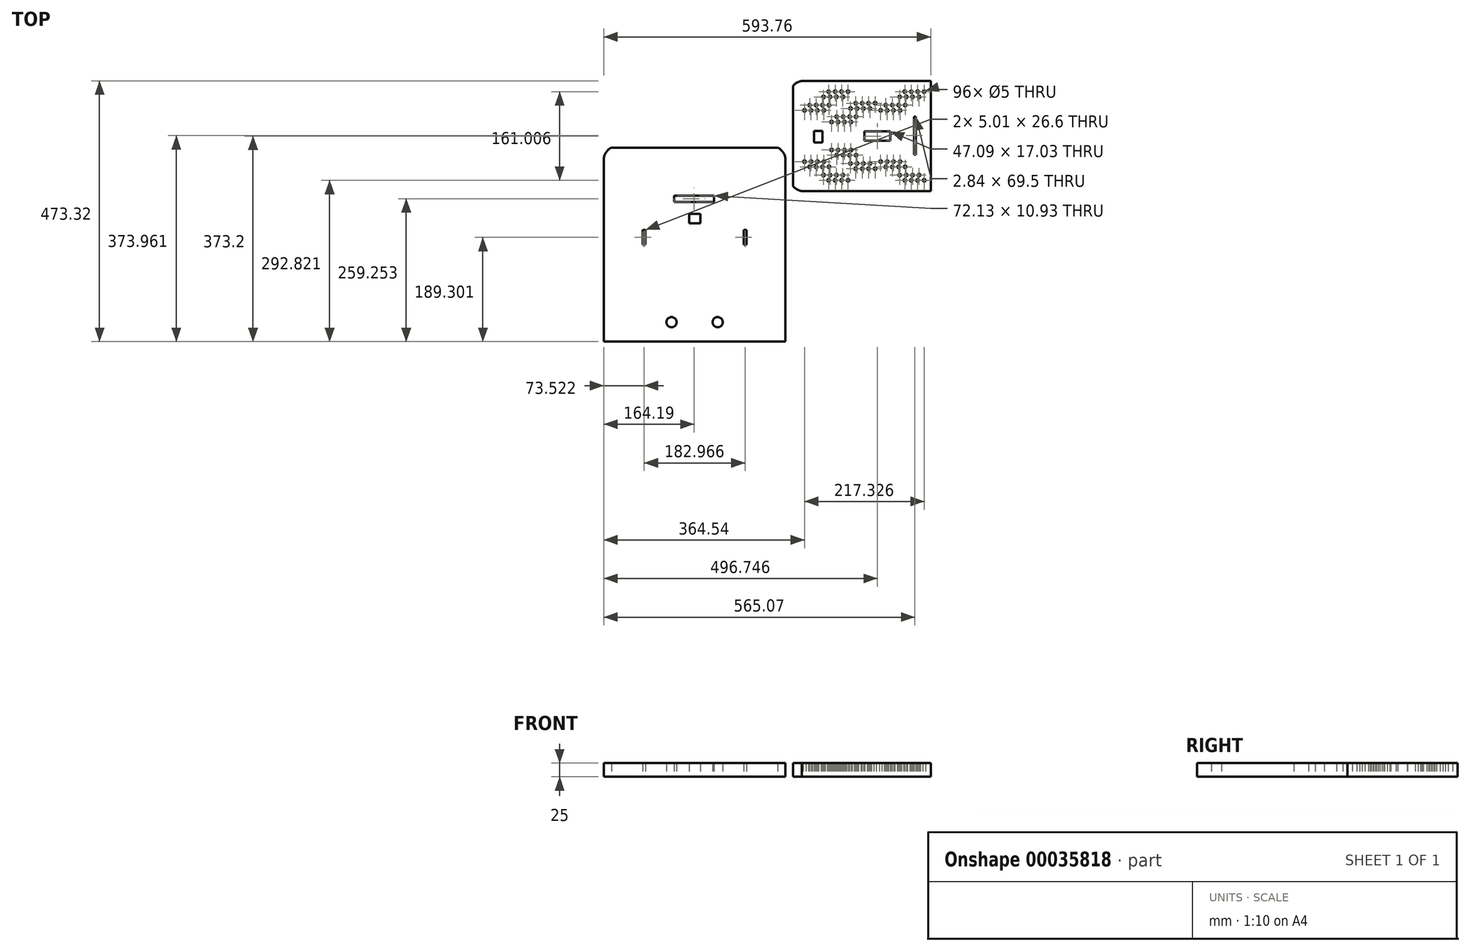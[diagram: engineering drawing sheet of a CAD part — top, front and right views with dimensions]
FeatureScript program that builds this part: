
annotation { "Feature Type Name" : "Feature", "Feature Type Description" : "" }
export const myFeature = defineFeature(function(context is Context, id is Id, definition is map)
    precondition{}
    {
        {
            var Q0;
            Q0=qCreatedBy(makeId("Top.planeOp"),FACE);
            var sketch = newSketch(context, id + "F0", { "sketchPlane" : qUnion([Q0])});
            skLineSegment(sketch, "E0.bottom", {"start": v(-545.13, 98.21) * mm, "end": v(-242.94, 98.21) * mm});
            skLineSegment(sketch, "E0.top", {"start": v(-559.04, -253.79) * mm, "end": v(-229.04, -253.79) * mm});
            skLineSegment(sketch, "E0.left", {"start": v(-559.04, 78.5) * mm, "end": v(-559.04, -253.79) * mm});
            skLineSegment(sketch, "E0.right", {"start": v(-229.04, 78.5) * mm, "end": v(-229.04, -253.79) * mm});
            skLineSegment(sketch, "E1", {"start": v(-394.04, 98.21) * mm, "end": v(-394.04, -253.79) * mm, "construction": true});
            skLineSegment(sketch, "E2.bottom", {"start": v(-430.92, 10.93) * mm, "end": v(-358.78, 10.93) * mm});
            skLineSegment(sketch, "E2.top", {"start": v(-430.92, 0) * mm, "end": v(-358.78, 0) * mm});
            skLineSegment(sketch, "E2.left", {"start": v(-430.92, 10.93) * mm, "end": v(-430.92, 0) * mm});
            skLineSegment(sketch, "E2.right", {"start": v(-358.78, 10.93) * mm, "end": v(-358.78, 0) * mm});
            skLineSegment(sketch, "E3.bottom", {"start": v(-403.87, -22.14) * mm, "end": v(-383.83, -22.14) * mm});
            skLineSegment(sketch, "E3.top", {"start": v(-403.87, -39.17) * mm, "end": v(-383.83, -39.17) * mm});
            skLineSegment(sketch, "E3.left", {"start": v(-403.87, -22.14) * mm, "end": v(-403.87, -39.17) * mm});
            skLineSegment(sketch, "E3.right", {"start": v(-383.83, -22.14) * mm, "end": v(-383.83, -39.17) * mm});
            skPoint(sketch, "E4.oppositeSnap0", {"position": v(-394.04, -77.79) * mm});
            skLineSegment(sketch, "E4.bottom", {"start": v(-488.02, -51.19) * mm, "end": v(-483.01, -51.19) * mm});
            skLineSegment(sketch, "E4.top", {"start": v(-488.02, -77.79) * mm, "end": v(-483.01, -77.79) * mm});
            skLineSegment(sketch, "E4.left", {"start": v(-488.02, -51.19) * mm, "end": v(-488.02, -77.79) * mm});
            skLineSegment(sketch, "E4.right", {"start": v(-483.01, -51.19) * mm, "end": v(-483.01, -77.79) * mm});
            skLineSegment(sketch, "E5.MirrorCS", {"start": v(-300.05, -51.19) * mm, "end": v(-305.06, -51.19) * mm});
            skLineSegment(sketch, "E6.MirrorCS", {"start": v(-300.05, -77.79) * mm, "end": v(-305.06, -77.79) * mm});
            skLineSegment(sketch, "E7.MirrorCS", {"start": v(-305.06, -51.19) * mm, "end": v(-305.06, -77.79) * mm});
            skLineSegment(sketch, "E8.MirrorCS", {"start": v(-300.05, -51.19) * mm, "end": v(-300.05, -77.79) * mm});
            skCircle(sketch, "E9", {"center": v(-435.93, -218.5) * mm, "radius": 9.24 * mm});
            skCircle(sketch, "E10.MirrorC", {"center": v(-352.14, -218.5) * mm, "radius": 9.24 * mm});
            skArc(sketch, "E11", {"start": v(-545.13, 98.21) * mm, "mid": v(-556.24, 87.33) * mm, "end": v(-559.04, 72.04) * mm});
            skArc(sketch, "E12.MirrorCS", {"start": v(-242.94, 98.21) * mm, "mid": v(-231.84, 87.33) * mm, "end": v(-229.04, 72.04) * mm});
            skSolve(sketch);
        }
        {
            var Q0;
            Q0=qCreatedBy(makeId("Top.planeOp"),FACE);
            var sketch = newSketch(context, id + "F1", { "sketchPlane" : qUnion([Q0])});
            skLineSegment(sketch, "E13.bottom", {"start": v(209.21, 93.3) * mm, "end": v(435.97, 93.3) * mm});
            skLineSegment(sketch, "E13.top", {"start": v(197.6, -206.7) * mm, "end": v(447.6, -206.7) * mm});
            skLineSegment(sketch, "E13.left", {"start": v(197.6, 76.54) * mm, "end": v(197.6, -206.7) * mm});
            skLineSegment(sketch, "E13.right", {"start": v(447.6, 76.54) * mm, "end": v(447.6, -206.7) * mm});
            skLineSegment(sketch, "E14", {"start": v(322.6, 93.3) * mm, "end": v(322.6, -206.7) * mm, "construction": true});
            skArc(sketch, "E15", {"start": v(209.21, 93.3) * mm, "mid": v(201.12, 86.5) * mm, "end": v(197.6, 76.54) * mm});
            skArc(sketch, "E16.MirrorCS", {"start": v(435.97, 93.3) * mm, "mid": v(444.06, 86.5) * mm, "end": v(447.6, 76.54) * mm});
            skCircle(sketch, "E17", {"center": v(230.31, 68.44) * mm, "radius": 2.5 * mm});
            skCircle(sketch, "E18", {"center": v(238.3, 68.31) * mm, "radius": 2.39 * mm});
            skCircle(sketch, "E19", {"center": v(245.98, 68.31) * mm, "radius": 2.5 * mm});
            skCircle(sketch, "E20", {"center": v(253.65, 68.31) * mm, "radius": 2.5 * mm});
            skCircle(sketch, "E21", {"center": v(246.06, 61.43) * mm, "radius": 2.5 * mm});
            skCircle(sketch, "E22", {"center": v(222.72, 61.56) * mm, "radius": 2.5 * mm});
            skCircle(sketch, "E23", {"center": v(230.71, 61.43) * mm, "radius": 2.39 * mm});
            skCircle(sketch, "E24", {"center": v(238.39, 61.43) * mm, "radius": 2.5 * mm});
            skCircle(sketch, "E25", {"center": v(238.66, 54.03) * mm, "radius": 2.5 * mm});
            skCircle(sketch, "E26", {"center": v(215.32, 54.16) * mm, "radius": 2.5 * mm});
            skCircle(sketch, "E27", {"center": v(223.31, 54.03) * mm, "radius": 2.39 * mm});
            skCircle(sketch, "E28", {"center": v(230.99, 54.03) * mm, "radius": 2.5 * mm});
            skCircle(sketch, "E29", {"center": v(278.95, 60.88) * mm, "radius": 2.5 * mm});
            skCircle(sketch, "E30", {"center": v(255.6, 61.01) * mm, "radius": 2.5 * mm});
            skCircle(sketch, "E31", {"center": v(263.6, 60.88) * mm, "radius": 2.39 * mm});
            skCircle(sketch, "E32", {"center": v(271.27, 60.88) * mm, "radius": 2.5 * mm});
            skCircle(sketch, "E33", {"center": v(285.25, 68.28) * mm, "radius": 2.5 * mm});
            skCircle(sketch, "E34", {"center": v(261.9, 68.41) * mm, "radius": 2.5 * mm});
            skCircle(sketch, "E35", {"center": v(269.9, 68.28) * mm, "radius": 2.39 * mm});
            skCircle(sketch, "E36", {"center": v(277.58, 68.28) * mm, "radius": 2.5 * mm});
            skCircle(sketch, "E37", {"center": v(281.41, 75.4) * mm, "radius": 2.5 * mm});
            skCircle(sketch, "E38", {"center": v(258.07, 75.54) * mm, "radius": 2.5 * mm});
            skCircle(sketch, "E39", {"center": v(266.07, 75.4) * mm, "radius": 2.39 * mm});
            skCircle(sketch, "E40", {"center": v(273.74, 75.4) * mm, "radius": 2.5 * mm});
            skCircle(sketch, "E41", {"center": v(296.4, 75.17) * mm, "radius": 2.5 * mm});
            skCircle(sketch, "E42", {"center": v(288.73, 75.17) * mm, "radius": 2.5 * mm});
            skCircle(sketch, "E43", {"center": v(260.89, 32.8) * mm, "radius": 2.5 * mm});
            skCircle(sketch, "E44", {"center": v(295.39, 39.55) * mm, "radius": 2.5 * mm});
            skCircle(sketch, "E45", {"center": v(262.58, 25.27) * mm, "radius": 2.39 * mm});
            skCircle(sketch, "E46", {"center": v(257.05, 39.92) * mm, "radius": 2.5 * mm});
            skCircle(sketch, "E47", {"center": v(280.4, 39.8) * mm, "radius": 2.5 * mm});
            skCircle(sketch, "E48", {"center": v(254.59, 25.4) * mm, "radius": 2.5 * mm});
            skCircle(sketch, "E49", {"center": v(245.04, 25.82) * mm, "radius": 2.5 * mm});
            skCircle(sketch, "E50", {"center": v(229.7, 25.82) * mm, "radius": 2.39 * mm});
            skCircle(sketch, "E51", {"center": v(272.72, 39.8) * mm, "radius": 2.5 * mm});
            skCircle(sketch, "E52", {"center": v(229.3, 32.83) * mm, "radius": 2.5 * mm});
            skCircle(sketch, "E53", {"center": v(237.64, 18.42) * mm, "radius": 2.5 * mm});
            skCircle(sketch, "E54", {"center": v(237.36, 25.82) * mm, "radius": 2.5 * mm});
            skCircle(sketch, "E55", {"center": v(244.96, 32.7) * mm, "radius": 2.5 * mm});
            skCircle(sketch, "E56", {"center": v(277.93, 25.27) * mm, "radius": 2.5 * mm});
            skCircle(sketch, "E57", {"center": v(229.96, 18.42) * mm, "radius": 2.5 * mm});
            skCircle(sketch, "E58", {"center": v(252.63, 32.7) * mm, "radius": 2.5 * mm});
            skCircle(sketch, "E59", {"center": v(270.25, 25.27) * mm, "radius": 2.5 * mm});
            skCircle(sketch, "E60", {"center": v(214.3, 18.55) * mm, "radius": 2.5 * mm});
            skCircle(sketch, "E61", {"center": v(287.71, 39.55) * mm, "radius": 2.5 * mm});
            skCircle(sketch, "E62", {"center": v(265.04, 39.8) * mm, "radius": 2.39 * mm});
            skCircle(sketch, "E63", {"center": v(276.55, 32.67) * mm, "radius": 2.5 * mm});
            skCircle(sketch, "E64", {"center": v(221.7, 25.95) * mm, "radius": 2.5 * mm});
            skCircle(sketch, "E65", {"center": v(268.88, 32.67) * mm, "radius": 2.39 * mm});
            skCircle(sketch, "E66", {"center": v(237.28, 32.7) * mm, "radius": 2.39 * mm});
            skCircle(sketch, "E67", {"center": v(222.3, 18.42) * mm, "radius": 2.39 * mm});
            skCircle(sketch, "E68", {"center": v(284.23, 32.67) * mm, "radius": 2.5 * mm});
            skCircle(sketch, "E69", {"center": v(259.78, -7.02) * mm, "radius": 2.5 * mm});
            skCircle(sketch, "E70", {"center": v(294.27, -0.26) * mm, "radius": 2.5 * mm});
            skCircle(sketch, "E71", {"center": v(261.47, -14.54) * mm, "radius": 2.39 * mm});
            skCircle(sketch, "E72", {"center": v(255.94, 0.11) * mm, "radius": 2.5 * mm});
            skCircle(sketch, "E73", {"center": v(279.28, -0.02) * mm, "radius": 2.5 * mm});
            skCircle(sketch, "E74", {"center": v(253.47, -14.42) * mm, "radius": 2.5 * mm});
            skCircle(sketch, "E75", {"center": v(243.93, -14) * mm, "radius": 2.5 * mm});
            skCircle(sketch, "E76", {"center": v(228.58, -14) * mm, "radius": 2.39 * mm});
            skCircle(sketch, "E77", {"center": v(271.6, -0.02) * mm, "radius": 2.5 * mm});
            skCircle(sketch, "E78", {"center": v(228.18, -6.98) * mm, "radius": 2.5 * mm});
            skCircle(sketch, "E79", {"center": v(236.53, -21.4) * mm, "radius": 2.5 * mm});
            skCircle(sketch, "E80", {"center": v(236.25, -14) * mm, "radius": 2.5 * mm});
            skCircle(sketch, "E81", {"center": v(243.85, -7.11) * mm, "radius": 2.5 * mm});
            skCircle(sketch, "E82", {"center": v(276.81, -14.54) * mm, "radius": 2.5 * mm});
            skCircle(sketch, "E83", {"center": v(228.85, -21.4) * mm, "radius": 2.5 * mm});
            skCircle(sketch, "E84", {"center": v(251.52, -7.11) * mm, "radius": 2.5 * mm});
            skCircle(sketch, "E85", {"center": v(269.14, -14.54) * mm, "radius": 2.5 * mm});
            skCircle(sketch, "E86", {"center": v(213.19, -21.27) * mm, "radius": 2.5 * mm});
            skCircle(sketch, "E87", {"center": v(286.6, -0.26) * mm, "radius": 2.5 * mm});
            skCircle(sketch, "E88", {"center": v(263.93, -0.02) * mm, "radius": 2.39 * mm});
            skCircle(sketch, "E89", {"center": v(275.44, -7.14) * mm, "radius": 2.5 * mm});
            skCircle(sketch, "E90", {"center": v(220.59, -13.87) * mm, "radius": 2.5 * mm});
            skCircle(sketch, "E91", {"center": v(267.77, -7.14) * mm, "radius": 2.39 * mm});
            skCircle(sketch, "E92", {"center": v(236.17, -7.11) * mm, "radius": 2.39 * mm});
            skCircle(sketch, "E93", {"center": v(221.18, -21.4) * mm, "radius": 2.39 * mm});
            skCircle(sketch, "E94", {"center": v(283.12, -7.14) * mm, "radius": 2.5 * mm});
            skCircle(sketch, "E95", {"center": v(259.12, -44.82) * mm, "radius": 2.5 * mm});
            skCircle(sketch, "E96", {"center": v(293.62, -38.07) * mm, "radius": 2.5 * mm});
            skCircle(sketch, "E97", {"center": v(260.81, -52.35) * mm, "radius": 2.39 * mm});
            skCircle(sketch, "E98", {"center": v(255.29, -37.7) * mm, "radius": 2.5 * mm});
            skCircle(sketch, "E99", {"center": v(278.63, -37.82) * mm, "radius": 2.5 * mm});
            skCircle(sketch, "E100", {"center": v(252.82, -52.22) * mm, "radius": 2.5 * mm});
            skCircle(sketch, "E101", {"center": v(243.27, -51.8) * mm, "radius": 2.5 * mm});
            skCircle(sketch, "E102", {"center": v(227.93, -51.8) * mm, "radius": 2.39 * mm});
            skCircle(sketch, "E103", {"center": v(270.95, -37.82) * mm, "radius": 2.5 * mm});
            skCircle(sketch, "E104", {"center": v(227.53, -44.79) * mm, "radius": 2.5 * mm});
            skCircle(sketch, "E105", {"center": v(235.87, -59.2) * mm, "radius": 2.5 * mm});
            skCircle(sketch, "E106", {"center": v(235.6, -51.8) * mm, "radius": 2.5 * mm});
            skCircle(sketch, "E107", {"center": v(243.2, -44.92) * mm, "radius": 2.5 * mm});
            skCircle(sketch, "E108", {"center": v(276.16, -52.35) * mm, "radius": 2.5 * mm});
            skCircle(sketch, "E109", {"center": v(228.2, -59.2) * mm, "radius": 2.5 * mm});
            skCircle(sketch, "E110", {"center": v(250.87, -44.92) * mm, "radius": 2.5 * mm});
            skCircle(sketch, "E111", {"center": v(268.49, -52.35) * mm, "radius": 2.5 * mm});
            skCircle(sketch, "E112", {"center": v(212.53, -59.07) * mm, "radius": 2.5 * mm});
            skCircle(sketch, "E113", {"center": v(285.95, -38.07) * mm, "radius": 2.5 * mm});
            skCircle(sketch, "E114", {"center": v(263.28, -37.82) * mm, "radius": 2.39 * mm});
            skCircle(sketch, "E115", {"center": v(274.8, -44.95) * mm, "radius": 2.5 * mm});
            skCircle(sketch, "E116", {"center": v(219.93, -51.67) * mm, "radius": 2.5 * mm});
            skCircle(sketch, "E117", {"center": v(267.12, -44.95) * mm, "radius": 2.39 * mm});
            skCircle(sketch, "E118", {"center": v(235.52, -44.92) * mm, "radius": 2.39 * mm});
            skCircle(sketch, "E119", {"center": v(220.53, -59.2) * mm, "radius": 2.39 * mm});
            skCircle(sketch, "E120", {"center": v(282.46, -44.95) * mm, "radius": 2.5 * mm});
            skCircle(sketch, "E121", {"center": v(262.06, -143.9) * mm, "radius": 2.5 * mm});
            skCircle(sketch, "E122", {"center": v(296.55, -137.14) * mm, "radius": 2.5 * mm});
            skCircle(sketch, "E123", {"center": v(263.75, -151.43) * mm, "radius": 2.39 * mm});
            skCircle(sketch, "E124", {"center": v(258.22, -136.77) * mm, "radius": 2.5 * mm});
            skCircle(sketch, "E125", {"center": v(281.56, -136.9) * mm, "radius": 2.5 * mm});
            skCircle(sketch, "E126", {"center": v(255.75, -151.3) * mm, "radius": 2.5 * mm});
            skCircle(sketch, "E127", {"center": v(246.2, -150.88) * mm, "radius": 2.5 * mm});
            skCircle(sketch, "E128", {"center": v(230.86, -150.88) * mm, "radius": 2.39 * mm});
            skCircle(sketch, "E129", {"center": v(273.89, -136.9) * mm, "radius": 2.5 * mm});
            skCircle(sketch, "E130", {"center": v(230.46, -143.87) * mm, "radius": 2.5 * mm});
            skCircle(sketch, "E131", {"center": v(238.8, -158.28) * mm, "radius": 2.5 * mm});
            skCircle(sketch, "E132", {"center": v(238.53, -150.88) * mm, "radius": 2.5 * mm});
            skCircle(sketch, "E133", {"center": v(246.13, -144) * mm, "radius": 2.5 * mm});
            skCircle(sketch, "E134", {"center": v(279.1, -151.43) * mm, "radius": 2.5 * mm});
            skCircle(sketch, "E135", {"center": v(231.13, -158.28) * mm, "radius": 2.5 * mm});
            skCircle(sketch, "E136", {"center": v(253.8, -144) * mm, "radius": 2.5 * mm});
            skCircle(sketch, "E137", {"center": v(271.42, -151.43) * mm, "radius": 2.5 * mm});
            skCircle(sketch, "E138", {"center": v(215.47, -158.15) * mm, "radius": 2.5 * mm});
            skCircle(sketch, "E139", {"center": v(288.88, -137.14) * mm, "radius": 2.5 * mm});
            skCircle(sketch, "E140", {"center": v(266.21, -136.9) * mm, "radius": 2.39 * mm});
            skCircle(sketch, "E141", {"center": v(277.72, -144.03) * mm, "radius": 2.5 * mm});
            skCircle(sketch, "E142", {"center": v(222.87, -150.75) * mm, "radius": 2.5 * mm});
            skCircle(sketch, "E143", {"center": v(270.05, -144.03) * mm, "radius": 2.39 * mm});
            skCircle(sketch, "E144", {"center": v(238.45, -144) * mm, "radius": 2.39 * mm});
            skCircle(sketch, "E145", {"center": v(223.46, -158.28) * mm, "radius": 2.39 * mm});
            skCircle(sketch, "E146", {"center": v(285.4, -144.03) * mm, "radius": 2.5 * mm});
            skCircle(sketch, "E147", {"center": v(231.11, -106.06) * mm, "radius": 2.5 * mm});
            skCircle(sketch, "E148", {"center": v(289.53, -99.34) * mm, "radius": 2.5 * mm});
            skCircle(sketch, "E149", {"center": v(264.4, -113.62) * mm, "radius": 2.39 * mm});
            skCircle(sketch, "E150", {"center": v(286.05, -106.22) * mm, "radius": 2.5 * mm});
            skCircle(sketch, "E151", {"center": v(254.45, -106.19) * mm, "radius": 2.5 * mm});
            skCircle(sketch, "E152", {"center": v(246.86, -113.07) * mm, "radius": 2.5 * mm});
            skCircle(sketch, "E153", {"center": v(279.75, -113.62) * mm, "radius": 2.5 * mm});
            skCircle(sketch, "E154", {"center": v(239.1, -106.19) * mm, "radius": 2.39 * mm});
            skCircle(sketch, "E155", {"center": v(231.51, -113.07) * mm, "radius": 2.39 * mm});
            skCircle(sketch, "E156", {"center": v(224.11, -120.47) * mm, "radius": 2.39 * mm});
            skCircle(sketch, "E157", {"center": v(274.54, -99.1) * mm, "radius": 2.5 * mm});
            skCircle(sketch, "E158", {"center": v(272.07, -113.62) * mm, "radius": 2.5 * mm});
            skCircle(sketch, "E159", {"center": v(262.7, -106.1) * mm, "radius": 2.5 * mm});
            skCircle(sketch, "E160", {"center": v(216.12, -120.34) * mm, "radius": 2.5 * mm});
            skCircle(sketch, "E161", {"center": v(297.2, -99.34) * mm, "radius": 2.5 * mm});
            skCircle(sketch, "E162", {"center": v(239.46, -120.47) * mm, "radius": 2.5 * mm});
            skCircle(sketch, "E163", {"center": v(266.87, -99.1) * mm, "radius": 2.39 * mm});
            skCircle(sketch, "E164", {"center": v(258.87, -98.97) * mm, "radius": 2.5 * mm});
            skCircle(sketch, "E165", {"center": v(239.19, -113.07) * mm, "radius": 2.5 * mm});
            skCircle(sketch, "E166", {"center": v(256.4, -113.5) * mm, "radius": 2.5 * mm});
            skCircle(sketch, "E167", {"center": v(223.52, -112.94) * mm, "radius": 2.5 * mm});
            skCircle(sketch, "E168", {"center": v(231.79, -120.47) * mm, "radius": 2.5 * mm});
            skCircle(sketch, "E169", {"center": v(246.78, -106.19) * mm, "radius": 2.5 * mm});
            skCircle(sketch, "E170", {"center": v(270.7, -106.22) * mm, "radius": 2.39 * mm});
            skCircle(sketch, "E171", {"center": v(278.38, -106.22) * mm, "radius": 2.5 * mm});
            skCircle(sketch, "E172", {"center": v(282.21, -99.1) * mm, "radius": 2.5 * mm});
            skCircle(sketch, "E173.MirrorC", {"center": v(374.48, -106.22) * mm, "radius": 2.39 * mm});
            skCircle(sketch, "E174.MirrorC", {"center": v(376.3, 32.67) * mm, "radius": 2.39 * mm});
            skCircle(sketch, "E175.MirrorC", {"center": v(400.23, 32.7) * mm, "radius": 2.5 * mm});
            skCircle(sketch, "E176.MirrorC", {"center": v(391.38, -144) * mm, "radius": 2.5 * mm});
            skCircle(sketch, "E177.MirrorC", {"center": v(384.3, 32.8) * mm, "radius": 2.5 * mm});
            skCircle(sketch, "E178.MirrorC", {"center": v(402, -44.92) * mm, "radius": 2.5 * mm});
            skCircle(sketch, "E179.MirrorC", {"center": v(362.97, -99.1) * mm, "radius": 2.5 * mm});
            skCircle(sketch, "E180.MirrorC", {"center": v(367.46, -144.03) * mm, "radius": 2.5 * mm});
            skCircle(sketch, "E181.MirrorC", {"center": v(424, -21.4) * mm, "radius": 2.39 * mm});
            skCircle(sketch, "E182.MirrorC", {"center": v(380.14, 39.8) * mm, "radius": 2.39 * mm});
            skCircle(sketch, "E183.MirrorC", {"center": v(394.32, -44.92) * mm, "radius": 2.5 * mm});
            skCircle(sketch, "E184.MirrorC", {"center": v(409.58, -51.8) * mm, "radius": 2.5 * mm});
            skCircle(sketch, "E185.MirrorC", {"center": v(382.48, -106.1) * mm, "radius": 2.5 * mm});
            skCircle(sketch, "E186.MirrorC", {"center": v(375.13, -144.03) * mm, "radius": 2.39 * mm});
            skCircle(sketch, "E187.MirrorC", {"center": v(378.97, -136.9) * mm, "radius": 2.39 * mm});
            skCircle(sketch, "E188.MirrorC", {"center": v(386.06, -44.82) * mm, "radius": 2.5 * mm});
            skCircle(sketch, "E189.MirrorC", {"center": v(372.47, 39.8) * mm, "radius": 2.5 * mm});
            skCircle(sketch, "E190.MirrorC", {"center": v(364.8, 39.8) * mm, "radius": 2.5 * mm});
            skCircle(sketch, "E191.MirrorC", {"center": v(392.55, 32.7) * mm, "radius": 2.5 * mm});
            skCircle(sketch, "E192.MirrorC", {"center": v(368.63, 32.67) * mm, "radius": 2.5 * mm});
            skCircle(sketch, "E193.MirrorC", {"center": v(373.76, -151.43) * mm, "radius": 2.5 * mm});
            skCircle(sketch, "E194.MirrorC", {"center": v(398.4, -106.19) * mm, "radius": 2.5 * mm});
            skCircle(sketch, "E195.MirrorC", {"center": v(365.9, -0.02) * mm, "radius": 2.5 * mm});
            skCircle(sketch, "E196.MirrorC", {"center": v(369.74, -7.14) * mm, "radius": 2.5 * mm});
            skCircle(sketch, "E197.MirrorC", {"center": v(383.13, -143.9) * mm, "radius": 2.5 * mm});
            skCircle(sketch, "E198.MirrorC", {"center": v(415.22, 18.42) * mm, "radius": 2.5 * mm});
            skCircle(sketch, "E199.MirrorC", {"center": v(414.72, -143.87) * mm, "radius": 2.5 * mm});
            skCircle(sketch, "E200.MirrorC", {"center": v(415.5, 25.82) * mm, "radius": 2.39 * mm});
            skCircle(sketch, "E201.MirrorC", {"center": v(407.9, 32.7) * mm, "radius": 2.39 * mm});
            skCircle(sketch, "E202.MirrorC", {"center": v(398.33, -113.07) * mm, "radius": 2.5 * mm});
            skCircle(sketch, "E203.MirrorC", {"center": v(413.4, -120.47) * mm, "radius": 2.5 * mm});
            skCircle(sketch, "E204.MirrorC", {"center": v(371.45, 75.4) * mm, "radius": 2.5 * mm});
            skCircle(sketch, "E205.MirrorC", {"center": v(409.66, -44.92) * mm, "radius": 2.39 * mm});
            skCircle(sketch, "E206.MirrorC", {"center": v(366.8, -106.22) * mm, "radius": 2.5 * mm});
            skCircle(sketch, "E207.MirrorC", {"center": v(377.42, -7.14) * mm, "radius": 2.39 * mm});
            skCircle(sketch, "E208.MirrorC", {"center": v(390.73, -106.19) * mm, "radius": 2.5 * mm});
            skCircle(sketch, "E209.MirrorC", {"center": v(399.06, -144) * mm, "radius": 2.5 * mm});
            skCircle(sketch, "E210.MirrorC", {"center": v(406.8, 61.43) * mm, "radius": 2.5 * mm});
            skCircle(sketch, "E211.MirrorC", {"center": v(406, -113.07) * mm, "radius": 2.5 * mm});
            skCircle(sketch, "E212.MirrorC", {"center": v(413.67, -113.07) * mm, "radius": 2.39 * mm});
            skCircle(sketch, "E213.MirrorC", {"center": v(406.73, -144) * mm, "radius": 2.39 * mm});
            skCircle(sketch, "E214.MirrorC", {"center": v(414.32, -150.88) * mm, "radius": 2.39 * mm});
            skCircle(sketch, "E215.MirrorC", {"center": v(359.94, 68.28) * mm, "radius": 2.5 * mm});
            skCircle(sketch, "E216.MirrorC", {"center": v(384.37, -52.35) * mm, "radius": 2.39 * mm});
            skCircle(sketch, "E217.MirrorC", {"center": v(401.34, -7.11) * mm, "radius": 2.5 * mm});
            skCircle(sketch, "E218.MirrorC", {"center": v(400.15, 25.82) * mm, "radius": 2.5 * mm});
            skCircle(sketch, "E219.MirrorC", {"center": v(347.98, -99.34) * mm, "radius": 2.5 * mm});
            skCircle(sketch, "E220.MirrorC", {"center": v(421.72, -158.28) * mm, "radius": 2.39 * mm});
            skCircle(sketch, "E221.MirrorC", {"center": v(371.3, -136.9) * mm, "radius": 2.5 * mm});
            skCircle(sketch, "E222.MirrorC", {"center": v(359.24, -38.07) * mm, "radius": 2.5 * mm});
            skCircle(sketch, "E223.MirrorC", {"center": v(383.28, 68.41) * mm, "radius": 2.5 * mm});
            skCircle(sketch, "E224.MirrorC", {"center": v(379.12, 75.4) * mm, "radius": 2.39 * mm});
            skCircle(sketch, "E225.MirrorC", {"center": v(421.67, -112.94) * mm, "radius": 2.5 * mm});
            skCircle(sketch, "E226.MirrorC", {"center": v(417.26, -51.8) * mm, "radius": 2.39 * mm});
            skCircle(sketch, "E227.MirrorC", {"center": v(417.66, -44.79) * mm, "radius": 2.5 * mm});
            skCircle(sketch, "E228.MirrorC", {"center": v(381.25, -0.02) * mm, "radius": 2.39 * mm});
            skCircle(sketch, "E229.MirrorC", {"center": v(365.44, -113.62) * mm, "radius": 2.5 * mm});
            skCircle(sketch, "E230.MirrorC", {"center": v(429.72, -158.15) * mm, "radius": 2.5 * mm});
            skCircle(sketch, "E231.MirrorC", {"center": v(421.87, 54.03) * mm, "radius": 2.39 * mm});
            skCircle(sketch, "E232.MirrorC", {"center": v(381.44, -151.43) * mm, "radius": 2.39 * mm});
            skCircle(sketch, "E233.MirrorC", {"center": v(369.02, -52.35) * mm, "radius": 2.5 * mm});
            skCircle(sketch, "E234.MirrorC", {"center": v(409.01, -7.11) * mm, "radius": 2.39 * mm});
            skCircle(sketch, "E235.MirrorC", {"center": v(416.6, -14) * mm, "radius": 2.39 * mm});
            skCircle(sketch, "E236.MirrorC", {"center": v(430.89, 18.55) * mm, "radius": 2.5 * mm});
            skCircle(sketch, "E237.MirrorC", {"center": v(349.8, 39.55) * mm, "radius": 2.5 * mm});
            skCircle(sketch, "E238.MirrorC", {"center": v(370.65, -99.1) * mm, "radius": 2.5 * mm});
            skCircle(sketch, "E239.MirrorC", {"center": v(416.98, -59.2) * mm, "radius": 2.5 * mm});
            skCircle(sketch, "E240.MirrorC", {"center": v(373.58, -0.02) * mm, "radius": 2.5 * mm});
            skCircle(sketch, "E241.MirrorC", {"center": v(389.58, 61.01) * mm, "radius": 2.5 * mm});
            skCircle(sketch, "E242.MirrorC", {"center": v(389.43, -151.3) * mm, "radius": 2.5 * mm});
            skCircle(sketch, "E243.MirrorC", {"center": v(362.07, -7.14) * mm, "radius": 2.5 * mm});
            skCircle(sketch, "E244.MirrorC", {"center": v(417, -6.98) * mm, "radius": 2.5 * mm});
            skCircle(sketch, "E245.MirrorC", {"center": v(373.11, -113.62) * mm, "radius": 2.5 * mm});
            skCircle(sketch, "E246.MirrorC", {"center": v(348.63, -137.14) * mm, "radius": 2.5 * mm});
            skCircle(sketch, "E247.MirrorC", {"center": v(370.4, -44.95) * mm, "radius": 2.5 * mm});
            skCircle(sketch, "E248.MirrorC", {"center": v(408.66, -21.4) * mm, "radius": 2.5 * mm});
            skCircle(sketch, "E249.MirrorC", {"center": v(424.6, -13.87) * mm, "radius": 2.5 * mm});
            skCircle(sketch, "E250.MirrorC", {"center": v(392.36, -52.22) * mm, "radius": 2.5 * mm});
            skCircle(sketch, "E251.MirrorC", {"center": v(367.6, 68.28) * mm, "radius": 2.5 * mm});
            skCircle(sketch, "E252.MirrorC", {"center": v(360.96, 32.67) * mm, "radius": 2.5 * mm});
            skCircle(sketch, "E253.MirrorC", {"center": v(393.66, -7.11) * mm, "radius": 2.5 * mm});
            skCircle(sketch, "E254.MirrorC", {"center": v(391.71, -14.42) * mm, "radius": 2.5 * mm});
            skCircle(sketch, "E255.MirrorC", {"center": v(415.9, 32.83) * mm, "radius": 2.5 * mm});
            skCircle(sketch, "E256.MirrorC", {"center": v(388.13, 39.92) * mm, "radius": 2.5 * mm});
            skCircle(sketch, "E257.MirrorC", {"center": v(363.62, -136.9) * mm, "radius": 2.5 * mm});
            skCircle(sketch, "E258.MirrorC", {"center": v(366.24, 60.88) * mm, "radius": 2.5 * mm});
            skCircle(sketch, "E259.MirrorC", {"center": v(382.6, 25.27) * mm, "radius": 2.39 * mm});
            skCircle(sketch, "E260.MirrorC", {"center": v(357.47, 39.55) * mm, "radius": 2.5 * mm});
            skCircle(sketch, "E261.MirrorC", {"center": v(429.87, 54.16) * mm, "radius": 2.5 * mm});
            skCircle(sketch, "E262.MirrorC", {"center": v(414.2, 54.03) * mm, "radius": 2.5 * mm});
            skCircle(sketch, "E263.MirrorC", {"center": v(356.45, 75.17) * mm, "radius": 2.5 * mm});
            skCircle(sketch, "E264.MirrorC", {"center": v(421.07, -120.47) * mm, "radius": 2.39 * mm});
            skCircle(sketch, "E265.MirrorC", {"center": v(386.96, -136.77) * mm, "radius": 2.5 * mm});
            skCircle(sketch, "E266.MirrorC", {"center": v(406.38, -158.28) * mm, "radius": 2.5 * mm});
            skCircle(sketch, "E267.MirrorC", {"center": v(414.07, -106.06) * mm, "radius": 2.5 * mm});
            skCircle(sketch, "E268.MirrorC", {"center": v(378.32, -99.1) * mm, "radius": 2.39 * mm});
            skCircle(sketch, "E269.MirrorC", {"center": v(376.7, -52.35) * mm, "radius": 2.5 * mm});
            skCircle(sketch, "E270.MirrorC", {"center": v(398.98, -150.88) * mm, "radius": 2.5 * mm});
            skCircle(sketch, "E271.MirrorC", {"center": v(381.59, 60.88) * mm, "radius": 2.39 * mm});
            skCircle(sketch, "E272.MirrorC", {"center": v(422.9, 18.42) * mm, "radius": 2.39 * mm});
            skCircle(sketch, "E273.MirrorC", {"center": v(416.33, -21.4) * mm, "radius": 2.5 * mm});
            skCircle(sketch, "E274.MirrorC", {"center": v(366.56, -37.82) * mm, "radius": 2.5 * mm});
            skCircle(sketch, "E275.MirrorC", {"center": v(375.28, 68.28) * mm, "radius": 2.39 * mm});
            skCircle(sketch, "E276.MirrorC", {"center": v(409.31, -59.2) * mm, "radius": 2.5 * mm});
            skCircle(sketch, "E277.MirrorC", {"center": v(348.78, 75.17) * mm, "radius": 2.5 * mm});
            skCircle(sketch, "E278.MirrorC", {"center": v(381.9, -37.82) * mm, "radius": 2.39 * mm});
            skCircle(sketch, "E279.MirrorC", {"center": v(359.79, -144.03) * mm, "radius": 2.5 * mm});
            skCircle(sketch, "E280.MirrorC", {"center": v(405.73, -120.47) * mm, "radius": 2.5 * mm});
            skCircle(sketch, "E281.MirrorC", {"center": v(389.25, 0.11) * mm, "radius": 2.5 * mm});
            skCircle(sketch, "E282.MirrorC", {"center": v(362.72, -44.95) * mm, "radius": 2.5 * mm});
            skCircle(sketch, "E283.MirrorC", {"center": v(422.47, 61.56) * mm, "radius": 2.5 * mm});
            skCircle(sketch, "E284.MirrorC", {"center": v(367.26, 25.27) * mm, "radius": 2.5 * mm});
            skCircle(sketch, "E285.MirrorC", {"center": v(399.13, 61.43) * mm, "radius": 2.5 * mm});
            skCircle(sketch, "E286.MirrorC", {"center": v(391.53, 68.31) * mm, "radius": 2.5 * mm});
            skCircle(sketch, "E287.MirrorC", {"center": v(366.1, -151.43) * mm, "radius": 2.5 * mm});
            skCircle(sketch, "E288.MirrorC", {"center": v(399.2, 68.31) * mm, "radius": 2.5 * mm});
            skCircle(sketch, "E289.MirrorC", {"center": v(407.82, 25.82) * mm, "radius": 2.5 * mm});
            skCircle(sketch, "E290.MirrorC", {"center": v(387.11, 75.54) * mm, "radius": 2.5 * mm});
            skCircle(sketch, "E291.MirrorC", {"center": v(414.05, -158.28) * mm, "radius": 2.5 * mm});
            skCircle(sketch, "E292.MirrorC", {"center": v(383.72, -14.54) * mm, "radius": 2.39 * mm});
            skCircle(sketch, "E293.MirrorC", {"center": v(374.23, -37.82) * mm, "radius": 2.5 * mm});
            skCircle(sketch, "E294.MirrorC", {"center": v(422.32, -150.75) * mm, "radius": 2.5 * mm});
            skCircle(sketch, "E295.MirrorC", {"center": v(407.55, 18.42) * mm, "radius": 2.5 * mm});
            skCircle(sketch, "E296.MirrorC", {"center": v(376.05, -14.54) * mm, "radius": 2.5 * mm});
            skCircle(sketch, "E297.MirrorC", {"center": v(429.07, -120.34) * mm, "radius": 2.5 * mm});
            skCircle(sketch, "E298.MirrorC", {"center": v(408.93, -14) * mm, "radius": 2.5 * mm});
            skCircle(sketch, "E299.MirrorC", {"center": v(351.56, -38.07) * mm, "radius": 2.5 * mm});
            skCircle(sketch, "E300.MirrorC", {"center": v(423.49, 25.95) * mm, "radius": 2.5 * mm});
            skCircle(sketch, "E301.MirrorC", {"center": v(432, -21.27) * mm, "radius": 2.5 * mm});
            skCircle(sketch, "E302.MirrorC", {"center": v(401.91, -51.8) * mm, "radius": 2.5 * mm});
            skCircle(sketch, "E303.MirrorC", {"center": v(380.79, -113.62) * mm, "radius": 2.39 * mm});
            skCircle(sketch, "E304.MirrorC", {"center": v(425.25, -51.67) * mm, "radius": 2.5 * mm});
            skCircle(sketch, "E305.MirrorC", {"center": v(374.93, 25.27) * mm, "radius": 2.5 * mm});
            skCircle(sketch, "E306.MirrorC", {"center": v(373.91, 60.88) * mm, "radius": 2.5 * mm});
            skCircle(sketch, "E307.MirrorC", {"center": v(388.78, -113.5) * mm, "radius": 2.5 * mm});
            skCircle(sketch, "E308.MirrorC", {"center": v(350.91, -0.26) * mm, "radius": 2.5 * mm});
            skCircle(sketch, "E309.MirrorC", {"center": v(414.47, 61.43) * mm, "radius": 2.39 * mm});
            skCircle(sketch, "E310.MirrorC", {"center": v(368.37, -14.54) * mm, "radius": 2.5 * mm});
            skCircle(sketch, "E311.MirrorC", {"center": v(356.3, -137.14) * mm, "radius": 2.5 * mm});
            skCircle(sketch, "E312.MirrorC", {"center": v(424.66, -59.2) * mm, "radius": 2.39 * mm});
            skCircle(sketch, "E313.MirrorC", {"center": v(363.77, 75.4) * mm, "radius": 2.5 * mm});
            skCircle(sketch, "E314.MirrorC", {"center": v(355.65, -99.34) * mm, "radius": 2.5 * mm});
            skCircle(sketch, "E315.MirrorC", {"center": v(406.88, 68.31) * mm, "radius": 2.39 * mm});
            skCircle(sketch, "E316.MirrorC", {"center": v(414.87, 68.44) * mm, "radius": 2.5 * mm});
            skCircle(sketch, "E317.MirrorC", {"center": v(386.31, -98.97) * mm, "radius": 2.5 * mm});
            skCircle(sketch, "E318.MirrorC", {"center": v(406.65, -150.88) * mm, "radius": 2.5 * mm});
            skCircle(sketch, "E319.MirrorC", {"center": v(390.6, 25.4) * mm, "radius": 2.5 * mm});
            skCircle(sketch, "E320.MirrorC", {"center": v(401.26, -14) * mm, "radius": 2.5 * mm});
            skCircle(sketch, "E321.MirrorC", {"center": v(389.9, -37.7) * mm, "radius": 2.5 * mm});
            skCircle(sketch, "E322.MirrorC", {"center": v(406.53, 54.03) * mm, "radius": 2.5 * mm});
            skCircle(sketch, "E323.MirrorC", {"center": v(378.07, -44.95) * mm, "radius": 2.39 * mm});
            skCircle(sketch, "E324.MirrorC", {"center": v(432.65, -59.07) * mm, "radius": 2.5 * mm});
            skCircle(sketch, "E325.MirrorC", {"center": v(406.08, -106.19) * mm, "radius": 2.39 * mm});
            skCircle(sketch, "E326.MirrorC", {"center": v(359.14, -106.22) * mm, "radius": 2.5 * mm});
            skCircle(sketch, "E327.MirrorC", {"center": v(385.4, -7.02) * mm, "radius": 2.5 * mm});
            skCircle(sketch, "E328.MirrorC", {"center": v(358.59, -0.26) * mm, "radius": 2.5 * mm});
            skPoint(sketch, "E329.oppositeSnap0", {"position": v(322.6, -56.7) * mm});
            skLineSegment(sketch, "E329.bottom", {"start": v(315.94, -9.87) * mm, "end": v(328.97, -9.87) * mm});
            skLineSegment(sketch, "E329.top", {"start": v(315.94, -56.7) * mm, "end": v(328.97, -56.7) * mm});
            skLineSegment(sketch, "E329.left", {"start": v(315.94, -9.87) * mm, "end": v(315.94, -56.7) * mm});
            skLineSegment(sketch, "E329.right", {"start": v(328.97, -9.87) * mm, "end": v(328.97, -56.7) * mm});
            skLineSegment(sketch, "E330.bottom", {"start": v(306.81, -149.36) * mm, "end": v(337.45, -149.36) * mm});
            skLineSegment(sketch, "E330.top", {"start": v(306.81, -153.92) * mm, "end": v(337.45, -153.92) * mm});
            skLineSegment(sketch, "E330.left", {"start": v(306.81, -149.36) * mm, "end": v(306.81, -153.92) * mm});
            skLineSegment(sketch, "E330.right", {"start": v(337.45, -149.36) * mm, "end": v(337.45, -153.92) * mm});
            skLineSegment(sketch, "E331.bottom", {"start": v(289.21, -172.17) * mm, "end": v(352.44, -172.17) * mm});
            skLineSegment(sketch, "E331.top", {"start": v(289.21, -181.95) * mm, "end": v(352.44, -181.95) * mm});
            skLineSegment(sketch, "E331.left", {"start": v(289.21, -172.17) * mm, "end": v(289.21, -181.95) * mm});
            skLineSegment(sketch, "E331.right", {"start": v(352.44, -172.17) * mm, "end": v(352.44, -181.95) * mm});
            skLineSegment(sketch, "E332.bottom", {"start": v(246.2, -71.14) * mm, "end": v(284.65, -71.14) * mm});
            skLineSegment(sketch, "E332.top", {"start": v(246.2, -75.7) * mm, "end": v(284.65, -75.7) * mm});
            skLineSegment(sketch, "E332.left", {"start": v(246.2, -71.14) * mm, "end": v(246.2, -75.7) * mm});
            skLineSegment(sketch, "E332.right", {"start": v(284.65, -71.14) * mm, "end": v(284.65, -75.7) * mm});
            skLineSegment(sketch, "E333.MirrorCS", {"start": v(360.53, -71.14) * mm, "end": v(360.53, -75.7) * mm});
            skLineSegment(sketch, "E334.MirrorCS", {"start": v(399, -71.14) * mm, "end": v(399, -75.7) * mm});
            skLineSegment(sketch, "E335.MirrorCS", {"start": v(399, -71.14) * mm, "end": v(360.53, -71.14) * mm});
            skLineSegment(sketch, "E336.MirrorCS", {"start": v(399, -75.7) * mm, "end": v(360.53, -75.7) * mm});
            skSolve(sketch);
        }
        {
            var Q0;
            Q0=qCreatedBy(makeId("Top.planeOp"),FACE);
            var sketch = newSketch(context, id + "F2", { "sketchPlane" : qUnion([Q0])});
            skLineSegment(sketch, "E337.bottom", {"start": v(-199.27, 219.53) * mm, "end": v(34.72, 219.53) * mm});
            skLineSegment(sketch, "E337.top", {"start": v(-199.27, 19.53) * mm, "end": v(34.72, 19.53) * mm});
            skLineSegment(sketch, "E337.left", {"start": v(-215.28, 210.55) * mm, "end": v(-215.28, 28.52) * mm});
            skLineSegment(sketch, "E337.right", {"start": v(34.72, 219.53) * mm, "end": v(34.72, 19.53) * mm});
            skCircle(sketch, "E338.MirrorC", {"center": v(230, -11.5) * mm, "radius": 2.5 * mm});
            skCircle(sketch, "E339.MirrorC", {"center": v(249.15, 65.11) * mm, "radius": 2.5 * mm});
            skCircle(sketch, "E340.MirrorC", {"center": v(227.6, -1.94) * mm, "radius": 2.5 * mm});
            skCircle(sketch, "E341.MirrorC", {"center": v(218.19, -11.5) * mm, "radius": 2.5 * mm});
            skCircle(sketch, "E342.MirrorC", {"center": v(259.2, 50.21) * mm, "radius": 2.5 * mm});
            skCircle(sketch, "E343.MirrorC", {"center": v(270.37, 74.67) * mm, "radius": 2.5 * mm});
            skCircle(sketch, "E344.MirrorC", {"center": v(250.94, -1.94) * mm, "radius": 2.5 * mm});
            skCircle(sketch, "E345.MirrorC", {"center": v(276.45, -44.4) * mm, "radius": 2.5 * mm});
            skCircle(sketch, "E346.MirrorC", {"center": v(276.03, 12.96) * mm, "radius": 2.5 * mm});
            skCircle(sketch, "E347.MirrorC", {"center": v(226.44, 40.65) * mm, "radius": 2.5 * mm});
            skCircle(sketch, "E348.MirrorC", {"center": v(244.33, -78.4) * mm, "radius": 2.5 * mm});
            skCircle(sketch, "E349.MirrorC", {"center": v(260.95, 65.11) * mm, "radius": 2.5 * mm});
            skCircle(sketch, "E350.MirrorC", {"center": v(249.78, 40.65) * mm, "radius": 2.5 * mm});
            skCircle(sketch, "E351.MirrorC", {"center": v(253.33, -11.5) * mm, "radius": 2.5 * mm});
            skCircle(sketch, "E352.MirrorC", {"center": v(230.42, -68.85) * mm, "radius": 2.5 * mm});
            skCircle(sketch, "E353.MirrorC", {"center": v(252.7, 12.96) * mm, "radius": 2.5 * mm});
            skCircle(sketch, "E354.MirrorC", {"center": v(247.39, 50.21) * mm, "radius": 2.5 * mm});
            skCircle(sketch, "E355.MirrorC", {"center": v(267.03, -53.95) * mm, "radius": 2.5 * mm});
            skCircle(sketch, "E356.MirrorC", {"center": v(232.52, -78.4) * mm, "radius": 2.5 * mm});
            skCircle(sketch, "E357.MirrorC", {"center": v(284.29, 65.11) * mm, "radius": 2.5 * mm});
            skCircle(sketch, "E358.MirrorC", {"center": v(241.94, -68.85) * mm, "radius": 2.5 * mm});
            skCircle(sketch, "E359.MirrorC", {"center": v(253.12, -44.4) * mm, "radius": 2.5 * mm});
            skCircle(sketch, "E360.MirrorC", {"center": v(293.7, 74.67) * mm, "radius": 2.5 * mm});
            skCircle(sketch, "E361.MirrorC", {"center": v(214.64, 40.65) * mm, "radius": 2.5 * mm});
            skCircle(sketch, "E362.MirrorC", {"center": v(241.52, -11.5) * mm, "radius": 2.5 * mm});
            skCircle(sketch, "E363.MirrorC", {"center": v(243.7, -53.95) * mm, "radius": 2.5 * mm});
            skCircle(sketch, "E364.MirrorC", {"center": v(262.11, 22.52) * mm, "radius": 2.5 * mm});
            skCircle(sketch, "E365.MirrorC", {"center": v(239.41, -1.94) * mm, "radius": 2.5 * mm});
            skCircle(sketch, "E366.MirrorC", {"center": v(272.48, 65.11) * mm, "radius": 2.5 * mm});
            skCircle(sketch, "E367.MirrorC", {"center": v(262.75, -1.94) * mm, "radius": 2.5 * mm});
            skCircle(sketch, "E368.MirrorC", {"center": v(218.6, -68.85) * mm, "radius": 2.5 * mm});
            skCircle(sketch, "E369.MirrorC", {"center": v(287.84, 12.96) * mm, "radius": 2.5 * mm});
            skCircle(sketch, "E370.MirrorC", {"center": v(209.19, -78.4) * mm, "radius": 2.5 * mm});
            skCircle(sketch, "E371.MirrorC", {"center": v(285.45, 22.52) * mm, "radius": 2.5 * mm});
            skCircle(sketch, "E372.MirrorC", {"center": v(297.26, 22.52) * mm, "radius": 2.5 * mm});
            skCircle(sketch, "E373.MirrorC", {"center": v(253.75, -68.85) * mm, "radius": 2.5 * mm});
            skCircle(sketch, "E374.MirrorC", {"center": v(224.05, 50.21) * mm, "radius": 2.5 * mm});
            skCircle(sketch, "E375.MirrorC", {"center": v(258.56, 74.67) * mm, "radius": 2.5 * mm});
            skCircle(sketch, "E376.MirrorC", {"center": v(278.84, -53.95) * mm, "radius": 2.5 * mm});
            skCircle(sketch, "E377.MirrorC", {"center": v(273.92, 22.52) * mm, "radius": 2.5 * mm});
            skCircle(sketch, "E378.MirrorC", {"center": v(221, -78.4) * mm, "radius": 2.5 * mm});
            skCircle(sketch, "E379.MirrorC", {"center": v(288.26, -44.4) * mm, "radius": 2.5 * mm});
            skCircle(sketch, "E380.MirrorC", {"center": v(264.92, -44.4) * mm, "radius": 2.5 * mm});
            skCircle(sketch, "E381.MirrorC", {"center": v(255.5, -53.95) * mm, "radius": 2.5 * mm});
            skCircle(sketch, "E382.MirrorC", {"center": v(237.97, 40.65) * mm, "radius": 2.5 * mm});
            skCircle(sketch, "E383.MirrorC", {"center": v(281.9, 74.67) * mm, "radius": 2.5 * mm});
            skCircle(sketch, "E384.MirrorC", {"center": v(235.86, 50.21) * mm, "radius": 2.5 * mm});
            skCircle(sketch, "E385.MirrorC", {"center": v(264.5, 12.96) * mm, "radius": 2.5 * mm});
            skCircle(sketch, "E386.MirrorC", {"center": v(212.22, -129) * mm, "radius": 2.5 * mm});
            skCircle(sketch, "E387.MirrorC", {"center": v(281.87, -104.55) * mm, "radius": 2.5 * mm});
            skCircle(sketch, "E388.MirrorC", {"center": v(256.14, -94.99) * mm, "radius": 2.5 * mm});
            skCircle(sketch, "E389.MirrorC", {"center": v(233.44, -119.45) * mm, "radius": 2.5 * mm});
            skCircle(sketch, "E390.MirrorC", {"center": v(221.63, -119.45) * mm, "radius": 2.5 * mm});
            skCircle(sketch, "E391.MirrorC", {"center": v(244.97, -119.45) * mm, "radius": 2.5 * mm});
            skCircle(sketch, "E392.MirrorC", {"center": v(256.78, -119.45) * mm, "radius": 2.5 * mm});
            skCircle(sketch, "E393.MirrorC", {"center": v(270.06, -104.55) * mm, "radius": 2.5 * mm});
            skCircle(sketch, "E394.MirrorC", {"center": v(235.55, -129) * mm, "radius": 2.5 * mm});
            skCircle(sketch, "E395.MirrorC", {"center": v(258.53, -104.55) * mm, "radius": 2.5 * mm});
            skCircle(sketch, "E396.MirrorC", {"center": v(247.36, -129) * mm, "radius": 2.5 * mm});
            skCircle(sketch, "E397.MirrorC", {"center": v(267.95, -94.99) * mm, "radius": 2.5 * mm});
            skCircle(sketch, "E398.MirrorC", {"center": v(246.73, -104.55) * mm, "radius": 2.5 * mm});
            skCircle(sketch, "E399.MirrorC", {"center": v(291.29, -94.99) * mm, "radius": 2.5 * mm});
            skCircle(sketch, "E400.MirrorC", {"center": v(279.48, -94.99) * mm, "radius": 2.5 * mm});
            skCircle(sketch, "E401.MirrorC", {"center": v(224.02, -129) * mm, "radius": 2.5 * mm});
            skCircle(sketch, "E402.MirrorC", {"center": v(215.2, -180.83) * mm, "radius": 2.5 * mm});
            skCircle(sketch, "E403.MirrorC", {"center": v(284.85, -156.37) * mm, "radius": 2.5 * mm});
            skCircle(sketch, "E404.MirrorC", {"center": v(259.12, -146.82) * mm, "radius": 2.5 * mm});
            skCircle(sketch, "E405.MirrorC", {"center": v(236.42, -171.27) * mm, "radius": 2.5 * mm});
            skCircle(sketch, "E406.MirrorC", {"center": v(224.61, -171.27) * mm, "radius": 2.5 * mm});
            skCircle(sketch, "E407.MirrorC", {"center": v(247.95, -171.27) * mm, "radius": 2.5 * mm});
            skCircle(sketch, "E408.MirrorC", {"center": v(259.76, -171.27) * mm, "radius": 2.5 * mm});
            skCircle(sketch, "E409.MirrorC", {"center": v(273.04, -156.37) * mm, "radius": 2.5 * mm});
            skCircle(sketch, "E410.MirrorC", {"center": v(238.53, -180.83) * mm, "radius": 2.5 * mm});
            skCircle(sketch, "E411.MirrorC", {"center": v(261.51, -156.37) * mm, "radius": 2.5 * mm});
            skCircle(sketch, "E412.MirrorC", {"center": v(250.34, -180.83) * mm, "radius": 2.5 * mm});
            skCircle(sketch, "E413.MirrorC", {"center": v(270.93, -146.82) * mm, "radius": 2.5 * mm});
            skCircle(sketch, "E414.MirrorC", {"center": v(249.7, -156.37) * mm, "radius": 2.5 * mm});
            skCircle(sketch, "E415.MirrorC", {"center": v(294.27, -146.82) * mm, "radius": 2.5 * mm});
            skCircle(sketch, "E416.MirrorC", {"center": v(282.46, -146.82) * mm, "radius": 2.5 * mm});
            skCircle(sketch, "E417.MirrorC", {"center": v(227, -180.83) * mm, "radius": 2.5 * mm});
            skCircle(sketch, "E418.MirrorC", {"center": v(377.23, -94.99) * mm, "radius": 2.5 * mm});
            skCircle(sketch, "E419.MirrorC", {"center": v(374.25, -146.82) * mm, "radius": 2.5 * mm});
            skCircle(sketch, "E420.MirrorC", {"center": v(384.23, 65.11) * mm, "radius": 2.5 * mm});
            skCircle(sketch, "E421.MirrorC", {"center": v(405.77, -1.94) * mm, "radius": 2.5 * mm});
            skCircle(sketch, "E422.MirrorC", {"center": v(389.68, -53.95) * mm, "radius": 2.5 * mm});
            skCircle(sketch, "E423.MirrorC", {"center": v(394.85, -180.83) * mm, "radius": 2.5 * mm});
            skCircle(sketch, "E424.MirrorC", {"center": v(397.83, -129) * mm, "radius": 2.5 * mm});
            skCircle(sketch, "E425.MirrorC", {"center": v(400.85, -78.4) * mm, "radius": 2.5 * mm});
            skCircle(sketch, "E426.MirrorC", {"center": v(383.07, 22.52) * mm, "radius": 2.5 * mm});
            skCircle(sketch, "E427.MirrorC", {"center": v(380.26, -44.4) * mm, "radius": 2.5 * mm});
            skCircle(sketch, "E428.MirrorC", {"center": v(421.16, -129) * mm, "radius": 2.5 * mm});
            skCircle(sketch, "E429.MirrorC", {"center": v(418.18, -180.83) * mm, "radius": 2.5 * mm});
            skCircle(sketch, "E430.MirrorC", {"center": v(386.65, -104.55) * mm, "radius": 2.5 * mm});
            skCircle(sketch, "E431.MirrorC", {"center": v(383.67, -156.37) * mm, "radius": 2.5 * mm});
            skCircle(sketch, "E432.MirrorC", {"center": v(418.74, 40.65) * mm, "radius": 2.5 * mm});
            skCircle(sketch, "E433.MirrorC", {"center": v(401.49, -53.95) * mm, "radius": 2.5 * mm});
            skCircle(sketch, "E434.MirrorC", {"center": v(356.93, -44.4) * mm, "radius": 2.5 * mm});
            skCircle(sketch, "E435.MirrorC", {"center": v(371.26, 22.52) * mm, "radius": 2.5 * mm});
            skCircle(sketch, "E436.MirrorC", {"center": v(375.12, -104.55) * mm, "radius": 2.5 * mm});
            skCircle(sketch, "E437.MirrorC", {"center": v(372.15, -156.37) * mm, "radius": 2.5 * mm});
            skCircle(sketch, "E438.MirrorC", {"center": v(368.73, -44.4) * mm, "radius": 2.5 * mm});
            skCircle(sketch, "E439.MirrorC", {"center": v(430.55, 40.65) * mm, "radius": 2.5 * mm});
            skCircle(sketch, "E440.MirrorC", {"center": v(403.66, -11.5) * mm, "radius": 2.5 * mm});
            skCircle(sketch, "E441.MirrorC", {"center": v(369.16, 12.96) * mm, "radius": 2.5 * mm});
            skCircle(sketch, "E442.MirrorC", {"center": v(424.19, -78.4) * mm, "radius": 2.5 * mm});
            skCircle(sketch, "E443.MirrorC", {"center": v(411.74, -119.45) * mm, "radius": 2.5 * mm});
            skCircle(sketch, "E444.MirrorC", {"center": v(408.76, -171.27) * mm, "radius": 2.5 * mm});
            skCircle(sketch, "E445.MirrorC", {"center": v(427, -11.5) * mm, "radius": 2.5 * mm});
            skCircle(sketch, "E446.MirrorC", {"center": v(360.9, 65.11) * mm, "radius": 2.5 * mm});
            skCircle(sketch, "E447.MirrorC", {"center": v(398.46, -104.55) * mm, "radius": 2.5 * mm});
            skCircle(sketch, "E448.MirrorC", {"center": v(395.48, -156.37) * mm, "radius": 2.5 * mm});
            skCircle(sketch, "E449.MirrorC", {"center": v(432.97, -129) * mm, "radius": 2.5 * mm});
            skCircle(sketch, "E450.MirrorC", {"center": v(407.21, 40.65) * mm, "radius": 2.5 * mm});
            skCircle(sketch, "E451.MirrorC", {"center": v(436, -78.4) * mm, "radius": 2.5 * mm});
            skCircle(sketch, "E452.MirrorC", {"center": v(397.8, 50.21) * mm, "radius": 2.5 * mm});
            skCircle(sketch, "E453.MirrorC", {"center": v(372.7, 65.11) * mm, "radius": 2.5 * mm});
            skCircle(sketch, "E454.MirrorC", {"center": v(415.2, -11.5) * mm, "radius": 2.5 * mm});
            skCircle(sketch, "E455.MirrorC", {"center": v(429.99, -180.83) * mm, "radius": 2.5 * mm});
            skCircle(sketch, "E456.MirrorC", {"center": v(382.44, -1.94) * mm, "radius": 2.5 * mm});
            skCircle(sketch, "E457.MirrorC", {"center": v(353.9, -94.99) * mm, "radius": 2.5 * mm});
            skCircle(sketch, "E458.MirrorC", {"center": v(417.58, -1.94) * mm, "radius": 2.5 * mm});
            skCircle(sketch, "E459.MirrorC", {"center": v(359.74, 22.52) * mm, "radius": 2.5 * mm});
            skCircle(sketch, "E460.MirrorC", {"center": v(350.92, -146.82) * mm, "radius": 2.5 * mm});
            skCircle(sketch, "E461.MirrorC", {"center": v(396.04, 65.11) * mm, "radius": 2.5 * mm});
            skCircle(sketch, "E462.MirrorC", {"center": v(360.34, -156.37) * mm, "radius": 2.5 * mm});
            skCircle(sketch, "E463.MirrorC", {"center": v(395.4, 40.65) * mm, "radius": 2.5 * mm});
            skCircle(sketch, "E464.MirrorC", {"center": v(380.68, 12.96) * mm, "radius": 2.5 * mm});
            skCircle(sketch, "E465.MirrorC", {"center": v(420.57, -171.27) * mm, "radius": 2.5 * mm});
            skCircle(sketch, "E466.MirrorC", {"center": v(366.34, -53.95) * mm, "radius": 2.5 * mm});
            skCircle(sketch, "E467.MirrorC", {"center": v(385.99, 50.21) * mm, "radius": 2.5 * mm});
            skCircle(sketch, "E468.MirrorC", {"center": v(385.43, -171.27) * mm, "radius": 2.5 * mm});
            skCircle(sketch, "E469.MirrorC", {"center": v(403.24, -68.85) * mm, "radius": 2.5 * mm});
            skCircle(sketch, "E470.MirrorC", {"center": v(351.48, 74.67) * mm, "radius": 2.5 * mm});
            skCircle(sketch, "E471.MirrorC", {"center": v(388.4, -119.45) * mm, "radius": 2.5 * mm});
            skCircle(sketch, "E472.MirrorC", {"center": v(394.25, -1.94) * mm, "radius": 2.5 * mm});
            skCircle(sketch, "E473.MirrorC", {"center": v(409.63, -129) * mm, "radius": 2.5 * mm});
            skCircle(sketch, "E474.MirrorC", {"center": v(386.62, 74.67) * mm, "radius": 2.5 * mm});
            skCircle(sketch, "E475.MirrorC", {"center": v(406.66, -180.83) * mm, "radius": 2.5 * mm});
            skCircle(sketch, "E476.MirrorC", {"center": v(397.24, -171.27) * mm, "radius": 2.5 * mm});
            skCircle(sketch, "E477.MirrorC", {"center": v(400.22, -119.45) * mm, "radius": 2.5 * mm});
            skCircle(sketch, "E478.MirrorC", {"center": v(362.73, -146.82) * mm, "radius": 2.5 * mm});
            skCircle(sketch, "E479.MirrorC", {"center": v(391.44, -68.85) * mm, "radius": 2.5 * mm});
            skCircle(sketch, "E480.MirrorC", {"center": v(421.13, 50.21) * mm, "radius": 2.5 * mm});
            skCircle(sketch, "E481.MirrorC", {"center": v(423.55, -119.45) * mm, "radius": 2.5 * mm});
            skCircle(sketch, "E482.MirrorC", {"center": v(363.29, 74.67) * mm, "radius": 2.5 * mm});
            skCircle(sketch, "E483.MirrorC", {"center": v(386.06, -146.82) * mm, "radius": 2.5 * mm});
            skCircle(sketch, "E484.MirrorC", {"center": v(378.15, -53.95) * mm, "radius": 2.5 * mm});
            skCircle(sketch, "E485.MirrorC", {"center": v(392.49, 12.96) * mm, "radius": 2.5 * mm});
            skCircle(sketch, "E486.MirrorC", {"center": v(374.81, 74.67) * mm, "radius": 2.5 * mm});
            skCircle(sketch, "E487.MirrorC", {"center": v(392.07, -44.4) * mm, "radius": 2.5 * mm});
            skCircle(sketch, "E488.MirrorC", {"center": v(363.32, -104.55) * mm, "radius": 2.5 * mm});
            skCircle(sketch, "E489.MirrorC", {"center": v(414.77, -68.85) * mm, "radius": 2.5 * mm});
            skCircle(sketch, "E490.MirrorC", {"center": v(412.66, -78.4) * mm, "radius": 2.5 * mm});
            skCircle(sketch, "E491.MirrorC", {"center": v(426.58, -68.85) * mm, "radius": 2.5 * mm});
            skCircle(sketch, "E492.MirrorC", {"center": v(365.7, -94.99) * mm, "radius": 2.5 * mm});
            skCircle(sketch, "E493.MirrorC", {"center": v(357.35, 12.96) * mm, "radius": 2.5 * mm});
            skCircle(sketch, "E494.MirrorC", {"center": v(347.93, 22.52) * mm, "radius": 2.5 * mm});
            skCircle(sketch, "E495.MirrorC", {"center": v(389.04, -94.99) * mm, "radius": 2.5 * mm});
            skCircle(sketch, "E496.MirrorC", {"center": v(391.86, -11.5) * mm, "radius": 2.5 * mm});
            skCircle(sketch, "E497.MirrorC", {"center": v(409.32, 50.21) * mm, "radius": 2.5 * mm});
            skLineSegment(sketch, "E498.bottom", {"start": v(314.9, 76.84) * mm, "end": v(330.39, 76.84) * mm});
            skLineSegment(sketch, "E498.top", {"start": v(314.9, 13.7) * mm, "end": v(330.39, 13.7) * mm});
            skLineSegment(sketch, "E498.left", {"start": v(314.9, 76.84) * mm, "end": v(314.9, 13.7) * mm});
            skLineSegment(sketch, "E498.right", {"start": v(330.39, 76.84) * mm, "end": v(330.39, 13.7) * mm});
            skLineSegment(sketch, "E499.bottom", {"start": v(319.07, -14.3) * mm, "end": v(326.22, -14.3) * mm});
            skLineSegment(sketch, "E499.top", {"start": v(319.07, -67.92) * mm, "end": v(326.22, -67.92) * mm});
            skLineSegment(sketch, "E499.left", {"start": v(319.07, -14.3) * mm, "end": v(319.07, -67.92) * mm});
            skLineSegment(sketch, "E499.right", {"start": v(326.22, -14.3) * mm, "end": v(326.22, -67.92) * mm});
            skLineSegment(sketch, "E500.bottom", {"start": v(320.26, -80.43) * mm, "end": v(325.02, -80.43) * mm});
            skLineSegment(sketch, "E500.top", {"start": v(320.26, -116.17) * mm, "end": v(325.02, -116.17) * mm});
            skLineSegment(sketch, "E500.left", {"start": v(320.26, -80.43) * mm, "end": v(320.26, -116.17) * mm});
            skLineSegment(sketch, "E500.right", {"start": v(325.02, -80.43) * mm, "end": v(325.02, -116.17) * mm});
            skLineSegment(sketch, "E501.bottom", {"start": v(309.54, -156.68) * mm, "end": v(335.75, -156.68) * mm});
            skLineSegment(sketch, "E501.top", {"start": v(309.54, -178.12) * mm, "end": v(335.75, -178.12) * mm});
            skLineSegment(sketch, "E501.left", {"start": v(309.54, -156.68) * mm, "end": v(309.54, -178.12) * mm});
            skLineSegment(sketch, "E501.right", {"start": v(335.75, -156.68) * mm, "end": v(335.75, -178.12) * mm});
            skLineSegment(sketch, "E502", {"start": v(-215.28, 119.53) * mm, "end": v(34.72, 119.53) * mm, "construction": true});
            skCircle(sketch, "E503.MirrorC", {"center": v(-161.75, 175.58) * mm, "radius": 2.5 * mm});
            skCircle(sketch, "E504.MirrorC", {"center": v(-138.76, 200.04) * mm, "radius": 2.5 * mm});
            skCircle(sketch, "E505.MirrorC", {"center": v(-194.5, 166.02) * mm, "radius": 2.5 * mm});
            skCircle(sketch, "E506.MirrorC", {"center": v(-115.43, 200.04) * mm, "radius": 2.5 * mm});
            skCircle(sketch, "E507.MirrorC", {"center": v(-182.7, 166.02) * mm, "radius": 2.5 * mm});
            skCircle(sketch, "E508.MirrorC", {"center": v(-150.57, 200.04) * mm, "radius": 2.5 * mm});
            skCircle(sketch, "E509.MirrorC", {"center": v(-148.18, 190.48) * mm, "radius": 2.5 * mm});
            skCircle(sketch, "E510.MirrorC", {"center": v(-173.27, 175.58) * mm, "radius": 2.5 * mm});
            skCircle(sketch, "E511.MirrorC", {"center": v(-127.24, 200.04) * mm, "radius": 2.5 * mm});
            skCircle(sketch, "E512.MirrorC", {"center": v(-136.66, 190.48) * mm, "radius": 2.5 * mm});
            skCircle(sketch, "E513.MirrorC", {"center": v(-171.17, 166.02) * mm, "radius": 2.5 * mm});
            skCircle(sketch, "E514.MirrorC", {"center": v(-159.36, 166.02) * mm, "radius": 2.5 * mm});
            skCircle(sketch, "E515.MirrorC", {"center": v(-185.08, 175.58) * mm, "radius": 2.5 * mm});
            skCircle(sketch, "E516.MirrorC", {"center": v(-124.85, 190.48) * mm, "radius": 2.5 * mm});
            skCircle(sketch, "E517.MirrorC", {"center": v(-149.94, 175.58) * mm, "radius": 2.5 * mm});
            skCircle(sketch, "E518.MirrorC", {"center": v(-160, 190.48) * mm, "radius": 2.5 * mm});
            skCircle(sketch, "E519.MirrorC", {"center": v(-112.66, 154.54) * mm, "radius": 2.5 * mm});
            skCircle(sketch, "E520.MirrorC", {"center": v(-89.67, 179) * mm, "radius": 2.5 * mm});
            skCircle(sketch, "E521.MirrorC", {"center": v(-145.4, 144.98) * mm, "radius": 2.5 * mm});
            skCircle(sketch, "E522.MirrorC", {"center": v(-66.34, 179) * mm, "radius": 2.5 * mm});
            skCircle(sketch, "E523.MirrorC", {"center": v(-133.6, 144.98) * mm, "radius": 2.5 * mm});
            skCircle(sketch, "E524.MirrorC", {"center": v(-101.48, 179) * mm, "radius": 2.5 * mm});
            skCircle(sketch, "E525.MirrorC", {"center": v(-99.1, 169.44) * mm, "radius": 2.5 * mm});
            skCircle(sketch, "E526.MirrorC", {"center": v(-124.18, 154.54) * mm, "radius": 2.5 * mm});
            skCircle(sketch, "E527.MirrorC", {"center": v(-78.15, 179) * mm, "radius": 2.5 * mm});
            skCircle(sketch, "E528.MirrorC", {"center": v(-87.57, 169.44) * mm, "radius": 2.5 * mm});
            skCircle(sketch, "E529.MirrorC", {"center": v(-122.07, 144.98) * mm, "radius": 2.5 * mm});
            skCircle(sketch, "E530.MirrorC", {"center": v(-110.27, 144.98) * mm, "radius": 2.5 * mm});
            skCircle(sketch, "E531.MirrorC", {"center": v(-136, 154.54) * mm, "radius": 2.5 * mm});
            skCircle(sketch, "E532.MirrorC", {"center": v(-75.76, 169.44) * mm, "radius": 2.5 * mm});
            skCircle(sketch, "E533.MirrorC", {"center": v(-100.85, 154.54) * mm, "radius": 2.5 * mm});
            skCircle(sketch, "E534.MirrorC", {"center": v(-110.9, 169.44) * mm, "radius": 2.5 * mm});
            skCircle(sketch, "E535.MirrorC", {"center": v(-23.5, 175.58) * mm, "radius": 2.5 * mm});
            skCircle(sketch, "E536.MirrorC", {"center": v(-0.5, 200.04) * mm, "radius": 2.5 * mm});
            skCircle(sketch, "E537.MirrorC", {"center": v(-56.24, 166.02) * mm, "radius": 2.5 * mm});
            skCircle(sketch, "E538.MirrorC", {"center": v(22.83, 200.04) * mm, "radius": 2.5 * mm});
            skCircle(sketch, "E539.MirrorC", {"center": v(-44.44, 166.02) * mm, "radius": 2.5 * mm});
            skCircle(sketch, "E540.MirrorC", {"center": v(-12.32, 200.04) * mm, "radius": 2.5 * mm});
            skCircle(sketch, "E541.MirrorC", {"center": v(-9.93, 190.48) * mm, "radius": 2.5 * mm});
            skCircle(sketch, "E542.MirrorC", {"center": v(-35.02, 175.58) * mm, "radius": 2.5 * mm});
            skCircle(sketch, "E543.MirrorC", {"center": v(11.02, 200.04) * mm, "radius": 2.5 * mm});
            skCircle(sketch, "E544.MirrorC", {"center": v(1.6, 190.48) * mm, "radius": 2.5 * mm});
            skCircle(sketch, "E545.MirrorC", {"center": v(-32.9, 166.02) * mm, "radius": 2.5 * mm});
            skCircle(sketch, "E546.MirrorC", {"center": v(-21.1, 166.02) * mm, "radius": 2.5 * mm});
            skCircle(sketch, "E547.MirrorC", {"center": v(-46.83, 175.58) * mm, "radius": 2.5 * mm});
            skCircle(sketch, "E548.MirrorC", {"center": v(13.4, 190.48) * mm, "radius": 2.5 * mm});
            skCircle(sketch, "E549.MirrorC", {"center": v(-11.68, 175.58) * mm, "radius": 2.5 * mm});
            skCircle(sketch, "E550.MirrorC", {"center": v(-21.73, 190.48) * mm, "radius": 2.5 * mm});
            skCircle(sketch, "E551.MirrorC", {"center": v(-182.7, 73.05) * mm, "radius": 2.5 * mm});
            skCircle(sketch, "E552.MirrorC", {"center": v(-173.27, 63.5) * mm, "radius": 2.5 * mm});
            skCircle(sketch, "E553.MirrorC", {"center": v(-87.57, 69.63) * mm, "radius": 2.5 * mm});
            skCircle(sketch, "E554.MirrorC", {"center": v(-133.6, 94.09) * mm, "radius": 2.5 * mm});
            skCircle(sketch, "E555.MirrorC", {"center": v(-99.1, 69.63) * mm, "radius": 2.5 * mm});
            skCircle(sketch, "E556.MirrorC", {"center": v(-148.18, 48.59) * mm, "radius": 2.5 * mm});
            skCircle(sketch, "E557.MirrorC", {"center": v(-124.18, 84.53) * mm, "radius": 2.5 * mm});
            skCircle(sketch, "E558.MirrorC", {"center": v(-161.75, 63.5) * mm, "radius": 2.5 * mm});
            skCircle(sketch, "E559.MirrorC", {"center": v(-112.66, 84.53) * mm, "radius": 2.5 * mm});
            skCircle(sketch, "E560.MirrorC", {"center": v(-171.17, 73.05) * mm, "radius": 2.5 * mm});
            skCircle(sketch, "E561.MirrorC", {"center": v(-136, 84.53) * mm, "radius": 2.5 * mm});
            skCircle(sketch, "E562.MirrorC", {"center": v(-75.76, 69.63) * mm, "radius": 2.5 * mm});
            skCircle(sketch, "E563.MirrorC", {"center": v(-124.85, 48.59) * mm, "radius": 2.5 * mm});
            skCircle(sketch, "E564.MirrorC", {"center": v(-115.43, 39.03) * mm, "radius": 2.5 * mm});
            skCircle(sketch, "E565.MirrorC", {"center": v(-149.94, 63.5) * mm, "radius": 2.5 * mm});
            skCircle(sketch, "E566.MirrorC", {"center": v(-138.76, 39.03) * mm, "radius": 2.5 * mm});
            skCircle(sketch, "E567.MirrorC", {"center": v(-89.67, 60.07) * mm, "radius": 2.5 * mm});
            skCircle(sketch, "E568.MirrorC", {"center": v(-101.48, 60.07) * mm, "radius": 2.5 * mm});
            skCircle(sketch, "E569.MirrorC", {"center": v(-66.34, 60.07) * mm, "radius": 2.5 * mm});
            skCircle(sketch, "E570.MirrorC", {"center": v(-136.66, 48.59) * mm, "radius": 2.5 * mm});
            skCircle(sketch, "E571.MirrorC", {"center": v(-145.4, 94.09) * mm, "radius": 2.5 * mm});
            skCircle(sketch, "E572.MirrorC", {"center": v(-194.5, 73.05) * mm, "radius": 2.5 * mm});
            skCircle(sketch, "E573.MirrorC", {"center": v(-100.85, 84.53) * mm, "radius": 2.5 * mm});
            skCircle(sketch, "E574.MirrorC", {"center": v(-110.9, 69.63) * mm, "radius": 2.5 * mm});
            skCircle(sketch, "E575.MirrorC", {"center": v(-127.24, 39.03) * mm, "radius": 2.5 * mm});
            skCircle(sketch, "E576.MirrorC", {"center": v(-78.15, 60.07) * mm, "radius": 2.5 * mm});
            skCircle(sketch, "E577.MirrorC", {"center": v(-160, 48.59) * mm, "radius": 2.5 * mm});
            skCircle(sketch, "E578.MirrorC", {"center": v(-122.07, 94.09) * mm, "radius": 2.5 * mm});
            skCircle(sketch, "E579.MirrorC", {"center": v(-185.08, 63.5) * mm, "radius": 2.5 * mm});
            skCircle(sketch, "E580.MirrorC", {"center": v(-110.27, 94.09) * mm, "radius": 2.5 * mm});
            skCircle(sketch, "E581.MirrorC", {"center": v(-150.57, 39.03) * mm, "radius": 2.5 * mm});
            skCircle(sketch, "E582.MirrorC", {"center": v(-159.36, 73.05) * mm, "radius": 2.5 * mm});
            skCircle(sketch, "E583.MirrorC", {"center": v(-21.73, 48.59) * mm, "radius": 2.5 * mm});
            skCircle(sketch, "E584.MirrorC", {"center": v(-11.68, 63.5) * mm, "radius": 2.5 * mm});
            skCircle(sketch, "E585.MirrorC", {"center": v(13.4, 48.59) * mm, "radius": 2.5 * mm});
            skCircle(sketch, "E586.MirrorC", {"center": v(-46.83, 63.5) * mm, "radius": 2.5 * mm});
            skCircle(sketch, "E587.MirrorC", {"center": v(-21.1, 73.05) * mm, "radius": 2.5 * mm});
            skCircle(sketch, "E588.MirrorC", {"center": v(-32.9, 73.05) * mm, "radius": 2.5 * mm});
            skCircle(sketch, "E589.MirrorC", {"center": v(1.6, 48.59) * mm, "radius": 2.5 * mm});
            skCircle(sketch, "E590.MirrorC", {"center": v(11.02, 39.03) * mm, "radius": 2.5 * mm});
            skCircle(sketch, "E591.MirrorC", {"center": v(-35.02, 63.5) * mm, "radius": 2.5 * mm});
            skCircle(sketch, "E592.MirrorC", {"center": v(-9.93, 48.59) * mm, "radius": 2.5 * mm});
            skCircle(sketch, "E593.MirrorC", {"center": v(-12.32, 39.03) * mm, "radius": 2.5 * mm});
            skCircle(sketch, "E594.MirrorC", {"center": v(-44.44, 73.05) * mm, "radius": 2.5 * mm});
            skCircle(sketch, "E595.MirrorC", {"center": v(22.83, 39.03) * mm, "radius": 2.5 * mm});
            skCircle(sketch, "E596.MirrorC", {"center": v(-56.24, 73.05) * mm, "radius": 2.5 * mm});
            skCircle(sketch, "E597.MirrorC", {"center": v(-0.5, 39.03) * mm, "radius": 2.5 * mm});
            skCircle(sketch, "E598.MirrorC", {"center": v(-23.5, 63.5) * mm, "radius": 2.5 * mm});
            skLineSegment(sketch, "E599.bottom", {"start": v(-177, 128.93) * mm, "end": v(-161.98, 128.93) * mm});
            skLineSegment(sketch, "E599.top", {"start": v(-177, 107.89) * mm, "end": v(-161.98, 107.89) * mm});
            skLineSegment(sketch, "E599.left", {"start": v(-177, 128.93) * mm, "end": v(-177, 107.89) * mm});
            skLineSegment(sketch, "E599.right", {"start": v(-161.98, 128.93) * mm, "end": v(-161.98, 107.89) * mm});
            skLineSegment(sketch, "E600.bottom", {"start": v(-85.84, 127.93) * mm, "end": v(-38.75, 127.93) * mm});
            skLineSegment(sketch, "E600.top", {"start": v(-85.84, 110.9) * mm, "end": v(-38.75, 110.9) * mm});
            skLineSegment(sketch, "E600.left", {"start": v(-85.84, 127.93) * mm, "end": v(-85.84, 110.9) * mm});
            skLineSegment(sketch, "E600.right", {"start": v(-38.75, 127.93) * mm, "end": v(-38.75, 110.9) * mm});
            skLineSegment(sketch, "E601.bottom", {"start": v(4.61, 154.92) * mm, "end": v(7.45, 154.92) * mm});
            skLineSegment(sketch, "E601.top", {"start": v(4.61, 85.42) * mm, "end": v(7.45, 85.42) * mm});
            skLineSegment(sketch, "E601.left", {"start": v(4.61, 154.92) * mm, "end": v(4.61, 85.42) * mm});
            skLineSegment(sketch, "E601.right", {"start": v(7.45, 154.92) * mm, "end": v(7.45, 85.42) * mm});
            skArc(sketch, "E602", {"start": v(-215.28, 28.52) * mm, "mid": v(-208.13, 22.5) * mm, "end": v(-199.27, 19.53) * mm});
            skArc(sketch, "E603.MirrorCS", {"start": v(-215.28, 210.55) * mm, "mid": v(-208.13, 216.57) * mm, "end": v(-199.27, 219.53) * mm});
            skSolve(sketch);
        }
        {
            var Q0;
            {var subQ3=sQuery(id+"F0.wireOp",EDGE,"E0.bottom");Q0=makeQuery(id+"F0.imprint","IMPRINT",FACE,{"disambiguationData":[TD([[makeQuery(id+"F0.imprint","IMPRINT",EDGE,{"derivedFrom":subQ3}),-1.0]])]});}
            extrude(context, id + "F3", {"entities" : qUnion([Q0]), "depth" : 25 * mm});
        }
        {
            var Q0;
            Q0=makeQuery(id+"F2.imprint","IMPRINT",FACE,{"disambiguationData":[TD([[makeQuery(id+"F2.imprint","IMPRINT",EDGE,{"derivedFrom":sQuery(id+"F2.wireOp",EDGE,"E337.bottom")}),-1.0]])]});
            extrude(context, id + "F4", {"entities" : qUnion([Q0]), "depth" : 25 * mm});
        }
    });
